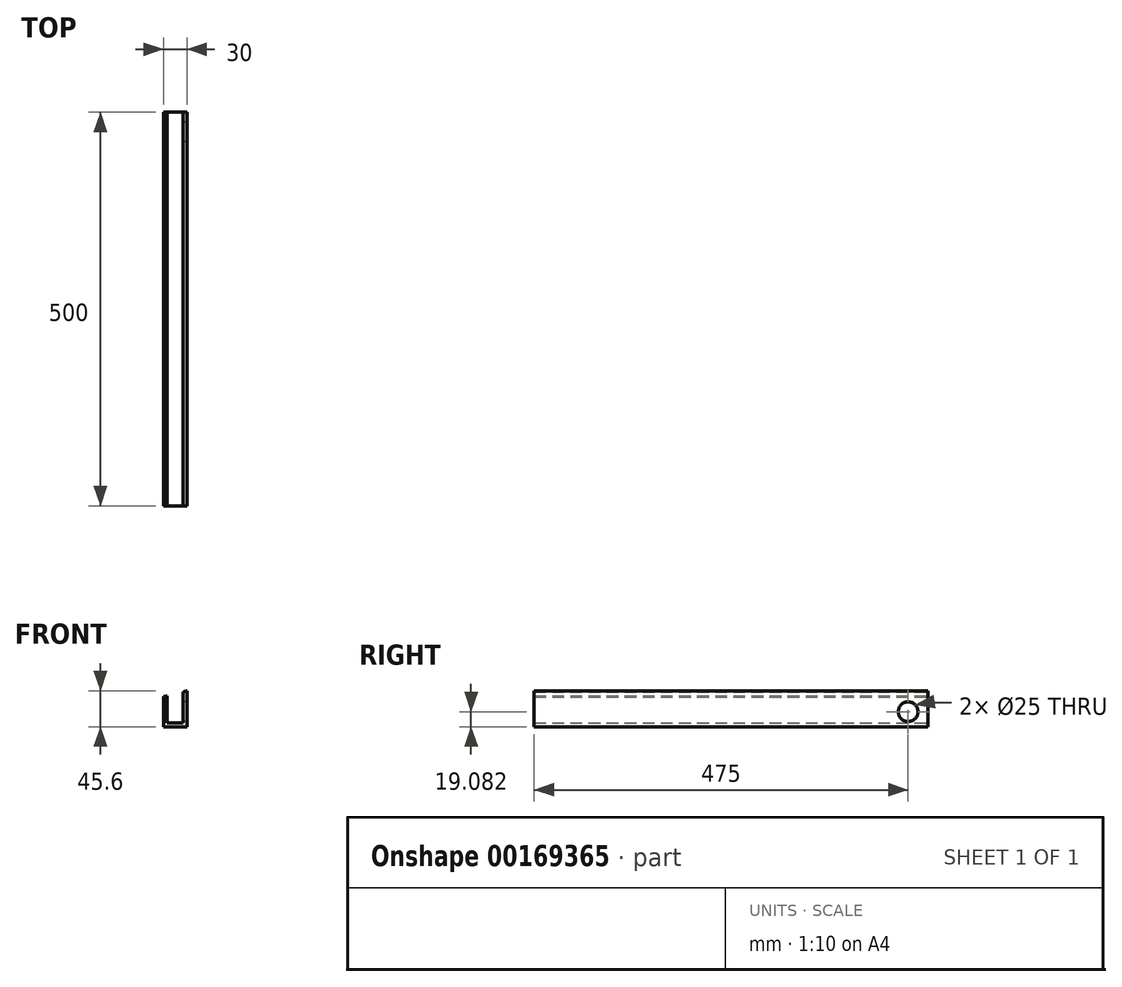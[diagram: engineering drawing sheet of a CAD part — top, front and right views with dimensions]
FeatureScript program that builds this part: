
annotation { "Feature Type Name" : "Feature", "Feature Type Description" : "" }
export const myFeature = defineFeature(function(context is Context, id is Id, definition is map)
    precondition{}
    {
        {
            var Q0;
            Q0=qCreatedBy(makeId("Front.planeOp"),FACE);
            var sketch = newSketch(context, id + "F0", { "sketchPlane" : qUnion([Q0])});
            skPoint(sketch, "E0", {"position": v(14.9, 14.26) * mm});
            skPoint(sketch, "E1", {"position": v(14.9, -23.9) * mm});
            skPoint(sketch, "E2", {"position": v(-15.1, -23.9) * mm});
            skLineSegment(sketch, "E3", {"start": v(-15.1, -23.9) * mm, "end": v(14.9, -23.9) * mm});
            skPoint(sketch, "E4", {"position": v(-10.1, -23.9) * mm});
            skPoint(sketch, "E5", {"position": v(9.9, -23.9) * mm});
            skPoint(sketch, "E6", {"position": v(-10.1, -18.9) * mm});
            skPoint(sketch, "E7", {"position": v(9.9, -18.9) * mm});
            skLineSegment(sketch, "E8", {"start": v(-10.1, -18.9) * mm, "end": v(9.9, -18.9) * mm});
            skPoint(sketch, "E9.MirrorP", {"position": v(15.1, -23.9) * mm});
            skPoint(sketch, "E10.MirrorP", {"position": v(-9.9, -23.9) * mm});
            skPoint(sketch, "E11.MirrorP", {"position": v(-9.9, -18.9) * mm});
            skPoint(sketch, "E12.MirrorP", {"position": v(-14.9, -23.9) * mm});
            skPoint(sketch, "E13.MirrorP", {"position": v(10.1, -23.9) * mm});
            skPoint(sketch, "E14.MirrorP", {"position": v(10.1, -18.9) * mm});
            skLineSegment(sketch, "E15.MirrorCS", {"start": v(10.1, -18.9) * mm, "end": v(-9.9, -18.9) * mm});
            skPoint(sketch, "E16.MirrorP", {"position": v(-14.9, 14.26) * mm});
            skLineSegment(sketch, "E17.MirrorCS", {"start": v(10.1, 20.2) * mm, "end": v(-9.9, 15.25) * mm});
            skLineSegment(sketch, "E18.MirrorCS", {"start": v(-9.9, -23.9) * mm, "end": v(-9.9, 15.25) * mm});
            skLineSegment(sketch, "E19.MirrorCS", {"start": v(10.1, -23.9) * mm, "end": v(10.1, 20.2) * mm});
            skLineSegment(sketch, "E20.MirrorCS", {"start": v(15.1, -23.9) * mm, "end": v(-14.9, -23.9) * mm});
            skArc(sketch, "E21.MirrorCS", {"start": v(15.1, 21.7) * mm, "mid": v(0.2, 17.54) * mm, "end": v(-14.9, 14.26) * mm});
            skLineSegment(sketch, "E22.MirrorCS", {"start": v(-14.9, 14.26) * mm, "end": v(-14.9, -23.9) * mm});
            skLineSegment(sketch, "E23.MirrorCS", {"start": v(15.1, -23.9) * mm, "end": v(15.1, 21.7) * mm});
            skPoint(sketch, "E24.MirrorP", {"position": v(15.1, 21.7) * mm});
            skSolve(sketch);
        }
        {
            var Q0;
            {var subQ3=sQuery(id+"F0.wireOp",EDGE,"E22.MirrorCS");Q0=makeQuery(id+"F0.imprint","IMPRINT",FACE,{"disambiguationData":[TD([[makeQuery(id+"F0.imprint","IMPRINT",EDGE,{"derivedFrom":subQ3}),1.0]])]});}
            var Q1;
            {var subQ1=sQuery(id+"F0.wireOp",EDGE,"E15.MirrorCS");var subQ8=makeQuery(id+"F0.imprint","IMPRINT",VERTEX,{"derivedFrom":subQ1});Q1=makeQuery(id+"F0.imprint","IMPRINT",FACE,{"disambiguationData":[TD([[makeQuery(id+"F0.imprint","IMPRINT",EDGE,{"disambiguationData":[TD([[subQ8,1.0]])],"derivedFrom":subQ1}),1.0]])]});}
            var Q2;
            {var subQ3=sQuery(id+"F0.wireOp",EDGE,"E23.MirrorCS");Q2=makeQuery(id+"F0.imprint","IMPRINT",FACE,{"disambiguationData":[TD([[makeQuery(id+"F0.imprint","IMPRINT",EDGE,{"derivedFrom":subQ3}),1.0]])]});}
            extrude(context, id + "F1", {"entities" : qUnion([Q0, Q1, Q2]), "depth" : 500 * mm});
        }
        {
            var Q0;
            Q0=makeQuery(id+"F1.opExtrude","SWEPT_FACE",FACE,{"disambiguationData":[OSD([sQuery(id+"F0.wireOp",EDGE,"E22.MirrorCS")])]});
            var sketch = newSketch(context, id + "F2", { "sketchPlane" : qUnion([Q0])});
            skPoint(sketch, "E25", {"position": v(0, 14.26) * mm});
            skPoint(sketch, "E26", {"position": v(50, 14.26) * mm});
            skPoint(sketch, "E27", {"position": v(50, -23.9) * mm});
            skPoint(sketch, "E28", {"position": v(0, -23.9) * mm});
            skLineSegment(sketch, "E29", {"start": v(0, 14.26) * mm, "end": v(0, -23.9) * mm});
            skLineSegment(sketch, "E30", {"start": v(0, 14.26) * mm, "end": v(50, 14.26) * mm});
            skPoint(sketch, "E31", {"position": v(25, 14.26) * mm});
            skPoint(sketch, "E32", {"position": v(0, -4.82) * mm});
            skPoint(sketch, "E33", {"position": v(25, -4.82) * mm});
            skCircle(sketch, "E34", {"center": v(25, -4.82) * mm, "radius": 12.5 * mm});
            skSolve(sketch);
        }
        {
            var Q0;
            Q0=makeQuery(id+"F2.imprint","IMPRINT",FACE,{"disambiguationData":[TD([[makeQuery(id+"F2.imprint","IMPRINT",EDGE,{"derivedFrom":sQuery(id+"F2.wireOp",EDGE,"E34")}),1.0]])]});
            extrude(context, id + "F3", {"entities" : qUnion([Q0]), "operationType" : NewBodyOperationType.REMOVE, "oppositeDirection" : true, "depth" : 800 * mm});
        }
    });
